# Revit family: Plumbing Fixture_WallgateWallgate_Wall_Button_CP-BS_CIPB12-B_W
name_source: partatom
category: Plumbing Fixtures
revit_build: Autodesk Revit 2017 (Build: 20160225_1515(x64)
units: mm (PartAtom-declared; Revit-internal decimal feet)

## family parameters
Cut with Voids When Loaded = No
Host = Face
Part Type = Normal
Room Calculation Point = No
Round Connector Dimension = Use Diameter
Shared = No

## types (1)
- Type 1
    Anti-Ligature = No
    Application = Commercial
    CW Connection = No
    Category/StyleorType_ANZRS = Plumbing Fixture
    DataSheet = https://www.galvinengineering.com.au
    Default Elevation = 1219 mm
    Description = Wallgate Secure WC Push Button For Pneumatic Cistern Cist19 PNEU-2; 25-190mm Wall-Single Push
    HW Connection = No
    Height = 0 mm  [stored 0 ft]
    Manufacturer = Wallgate
    Manufacturer_Overall Depth = 0 mm  [stored 0 ft]
    Manufacturer_Overall Height = 0 mm  [stored 0 ft]
    Manufacturer_Overall Width = 0 mm  [stored 0 ft]
    Mounting = Wall
    Mounting Surface = Wall
    Plumbing Finish = Chrome
    PlumbingMaterial_ANZRS = Brass
    Product Range (Series) = Wallgate
    Product Type = Push Button
    SKU = CIPB12-B
    Specify Host = Face
    URL = http://www.galvinengineering.com.au
    Vandal Resistant = No
    Vent Connection = No
    Waste Connection = No

note: [stored X ft] marks values corroborated as IEEE doubles in the binary element streams (Revit-internal decimal feet)

## geometry (parser evidence)
native form markers: Sweep x16
no freeform markers — native parametric forms only
